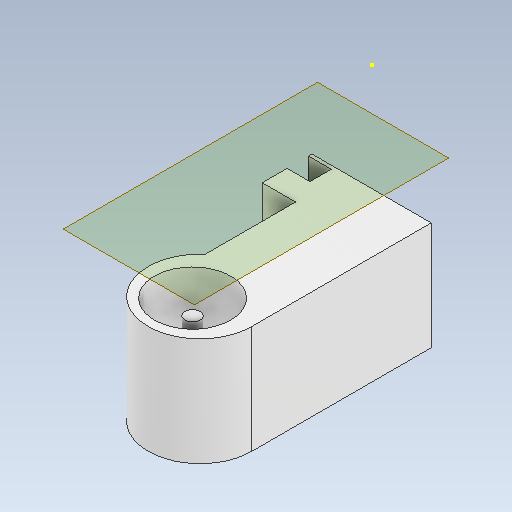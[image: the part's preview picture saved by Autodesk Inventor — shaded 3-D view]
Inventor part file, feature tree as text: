
AUTODESK INVENTOR PART (.ipt)
format: ipt  version: 2021 (Build 250183000, 183)  size: 123,392 bytes
history: native  units: mm
features: other x3, sketch x1, plane x1
ambient origin geometry x8: Origin, YZ Plane, XZ Plane, XY Plane, X Axis, Y Axis, Z Axis, Center Point
bodies: Solid1 (feature_tree)
feature tree (5):
  other  "leGs final.ipt"
  other  "Solid1::leGs final.ipt"
  other  "TaggingFeature1"
  sketch  "Sketch5"  dims[d0=30.0mm]
  plane  "Work Plane1"
